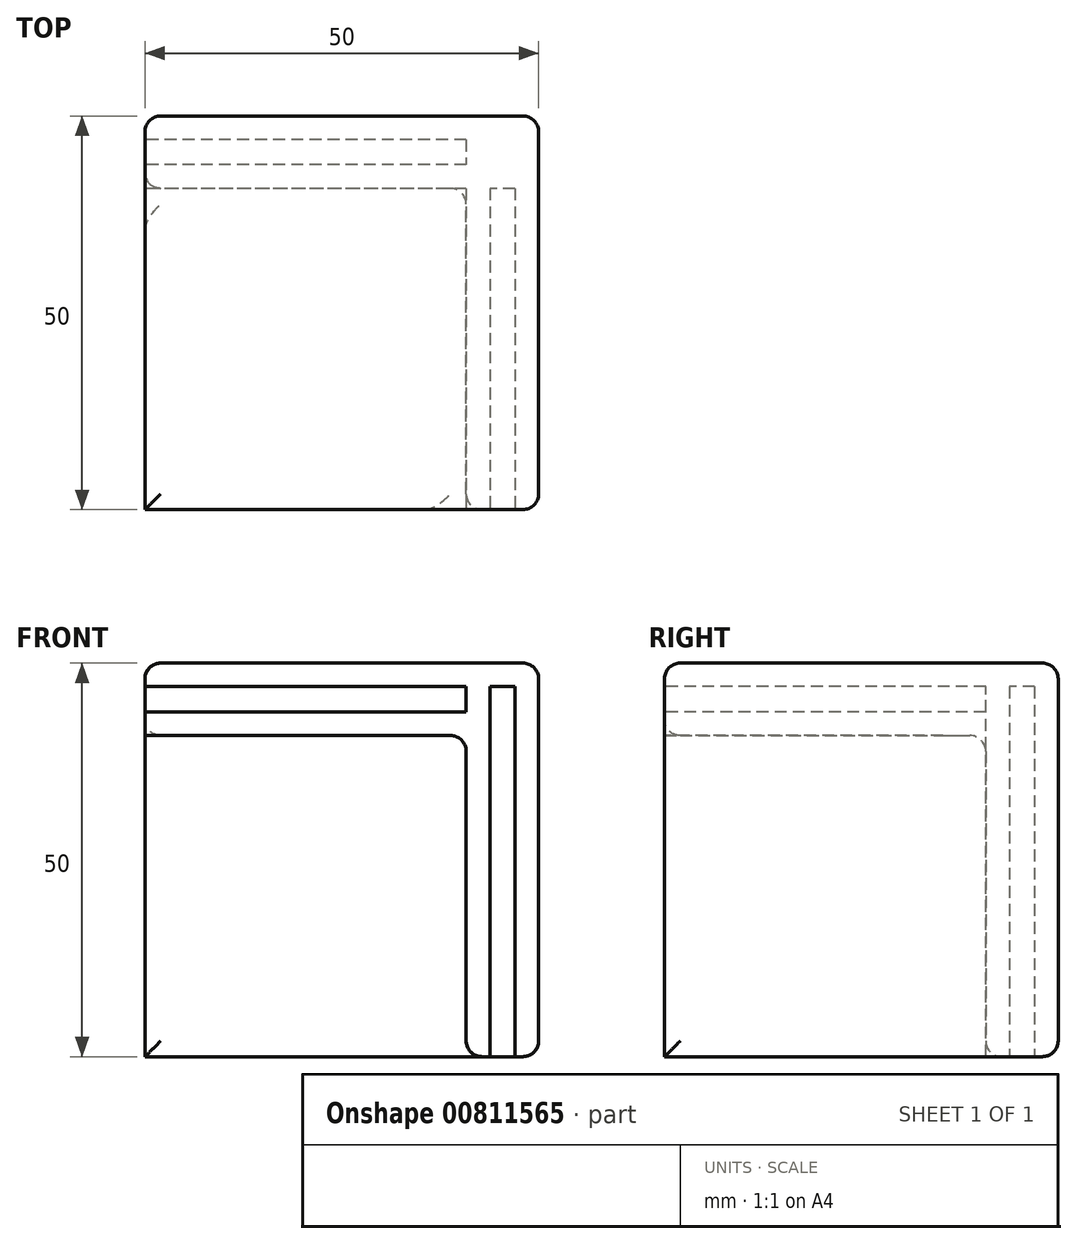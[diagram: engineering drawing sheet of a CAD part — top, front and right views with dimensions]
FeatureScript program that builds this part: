
annotation { "Feature Type Name" : "Feature", "Feature Type Description" : "" }
export const myFeature = defineFeature(function(context is Context, id is Id, definition is map)
    precondition{}
    {
        {
            var Q0;
            Q0=qCreatedBy(makeId("Top.planeOp"),FACE);
            var sketch = newSketch(context, id + "F0", { "sketchPlane" : qUnion([Q0])});
            skLineSegment(sketch, "E0.bottom", {"start": v(25, -25) * mm, "end": v(-25, -25) * mm});
            skLineSegment(sketch, "E0.top", {"start": v(25, 25) * mm, "end": v(-25, 25) * mm});
            skLineSegment(sketch, "E0.left", {"start": v(25, -25) * mm, "end": v(25, 25) * mm});
            skLineSegment(sketch, "E0.right", {"start": v(-25, -25) * mm, "end": v(-25, 25) * mm});
            skPoint(sketch, "E0.middle", {"position": v(0, 0) * mm});
            skSolve(sketch);
        }
        {
            var Q0;
            Q0=makeQuery(id+"F0.imprint","IMPRINT",FACE,{"disambiguationData":[TD([[makeQuery(id+"F0.imprint","IMPRINT",EDGE,{"derivedFrom":sQuery(id+"F0.wireOp",EDGE,"E0.bottom")}),-1.0]])]});
            extrude(context, id + "F1", {"entities" : qUnion([Q0]), "depth" : 3 * mm, "offsetDistance" : 25 * mm});
        }
        {
            var Q0;
            Q0=makeQuery(id+"F1.opExtrude","SWEPT_FACE",FACE,{"disambiguationData":[OSD([sQuery(id+"F0.wireOp",EDGE,"E0.right")])]});
            var sketch = newSketch(context, id + "F2", { "sketchPlane" : qUnion([Q0])});
            skLineSegment(sketch, "E1.bottom", {"start": v(-25, 3) * mm, "end": v(-22, 3) * mm});
            skLineSegment(sketch, "E1.top", {"start": v(-25, -47) * mm, "end": v(-22, -47) * mm});
            skLineSegment(sketch, "E1.left", {"start": v(-25, 3) * mm, "end": v(-25, -47) * mm});
            skLineSegment(sketch, "E1.right", {"start": v(-22, 3) * mm, "end": v(-22, -47) * mm});
            skLineSegment(sketch, "E2.bottom", {"start": v(-18.8, 3) * mm, "end": v(-15.8, 3) * mm});
            skLineSegment(sketch, "E2.top", {"start": v(-18.8, -47) * mm, "end": v(-15.8, -47) * mm});
            skLineSegment(sketch, "E2.left", {"start": v(-18.8, 3) * mm, "end": v(-18.8, -47) * mm});
            skLineSegment(sketch, "E2.right", {"start": v(-15.8, 3) * mm, "end": v(-15.8, -47) * mm});
            skSolve(sketch);
        }
        {
            var Q0;
            {var subQ0=sQuery(id+"F2.wireOp",EDGE,"E1.bottom");Q0=makeQuery(id+"F2.imprint","IMPRINT",FACE,{"disambiguationData":[TD([[makeQuery(id+"F2.imprint","IMPRINT",EDGE,{"derivedFrom":subQ0}),1.0]])]});}
            var Q1;
            {var subQ0=sQuery(id+"F2.wireOp",EDGE,"E2.bottom");Q1=makeQuery(id+"F2.imprint","IMPRINT",FACE,{"disambiguationData":[TD([[makeQuery(id+"F2.imprint","IMPRINT",EDGE,{"derivedFrom":subQ0}),1.0]])]});}
            var Q2;
            {var subQ0=sQuery(id+"F2.wireOp",EDGE,"E2.top");Q2=makeQuery(id+"F2.imprint","IMPRINT",FACE,{"disambiguationData":[TD([[makeQuery(id+"F2.imprint","IMPRINT",EDGE,{"derivedFrom":subQ0}),1.0]])]});}
            var Q3;
            {var subQ0=sQuery(id+"F2.wireOp",EDGE,"E1.top");Q3=makeQuery(id+"F2.imprint","IMPRINT",FACE,{"disambiguationData":[TD([[makeQuery(id+"F2.imprint","IMPRINT",EDGE,{"derivedFrom":subQ0}),1.0]])]});}
            var Q4;
            Q4=makeQuery(id+"F1.opExtrude","SWEPT_FACE",FACE,{"disambiguationData":[OSD([sQuery(id+"F0.wireOp",EDGE,"E0.left")])]});
            extrude(context, id + "F3", {"entities" : qUnion([Q0, Q1, Q2, Q3]), "operationType" : NewBodyOperationType.ADD, "endBound" : BoundingType.UP_TO_SURFACE, "oppositeDirection" : true, "depth" : 25 * mm, "endBoundEntityFace" : qUnion([Q4]), "offsetDistance" : 25 * mm});
        }
        {
            var Q0;
            Q0=makeQuery(id+"F1.opExtrude","SWEPT_FACE",FACE,{"disambiguationData":[OSD([sQuery(id+"F0.wireOp",EDGE,"E0.bottom")])]});
            var sketch = newSketch(context, id + "F4", { "sketchPlane" : qUnion([Q0])});
            skLineSegment(sketch, "E3.bottom", {"start": v(25, 3) * mm, "end": v(22, 3) * mm});
            skLineSegment(sketch, "E3.top", {"start": v(25, -47) * mm, "end": v(22, -47) * mm});
            skLineSegment(sketch, "E3.left", {"start": v(25, 3) * mm, "end": v(25, -47) * mm});
            skLineSegment(sketch, "E3.right", {"start": v(22, 3) * mm, "end": v(22, -47) * mm});
            skLineSegment(sketch, "E4.bottom", {"start": v(18.8, 3) * mm, "end": v(15.8, 3) * mm});
            skLineSegment(sketch, "E4.top", {"start": v(18.8, -47) * mm, "end": v(15.8, -47) * mm});
            skLineSegment(sketch, "E4.left", {"start": v(18.8, 3) * mm, "end": v(18.8, -47) * mm});
            skLineSegment(sketch, "E4.right", {"start": v(15.8, 3) * mm, "end": v(15.8, -47) * mm});
            skSolve(sketch);
        }
        {
            var Q0;
            Q0 = qSketchRegion(id + "F4", true);
            var Q1;
            Q1=makeQuery(id+"F3.opExtrude","SWEPT_FACE",FACE,{"disambiguationData":[OSD([sQuery(id+"F2.wireOp",EDGE,"E1.right")])]});
            extrude(context, id + "F5", {"entities" : qUnion([Q0]), "operationType" : NewBodyOperationType.ADD, "endBound" : BoundingType.UP_TO_SURFACE, "oppositeDirection" : true, "depth" : 25 * mm, "endBoundEntityFace" : qUnion([Q1]), "offsetDistance" : 25 * mm});
        }
        {
            var Q0;
            {var subQ0=sQuery(id+"F2.wireOp",EDGE,"E1.right");var subQ1=makeQuery(id+"F3.opExtrude","SWEPT_FACE",FACE,{"disambiguationData":[OSD([subQ0])]});var subQ7=sQuery(id+"F0.wireOp",EDGE,"E0.right");var subQ8=sQuery(id+"F0.wireOp",EDGE,"E0.left");Q0=makeQuery(id+"F5.boolean.opBoolean","SPLIT",FACE,{"disambiguationData":[TD([makeQuery(id+"F5.opExtrude","SWEPT_FACE",FACE,{"disambiguationData":[OSD([sQuery(id+"F4.wireOp",EDGE,"E3.right")])]})])],"derivedFrom":makeQuery(id+"F3.boolean.opBoolean","SPLIT",FACE,{"disambiguationData":[TD([subQ1])],"derivedFrom":makeQuery(id+"F1.opExtrude","CAP_FACE",FACE,{"disambiguationData":[OSD([sQuery(id+"F0.wireOp",EDGE,"E0.bottom"),sQuery(id+"F0.wireOp",EDGE,"E0.top"),subQ8,subQ7])],"isStart":true})})});}
            var Q1;
            Q1=makeQuery(id+"F1.opExtrude","CAP_FACE",FACE,{"disambiguationData":[OSD([sQuery(id+"F0.wireOp",EDGE,"E0.bottom"),sQuery(id+"F0.wireOp",EDGE,"E0.top"),sQuery(id+"F0.wireOp",EDGE,"E0.left"),sQuery(id+"F0.wireOp",EDGE,"E0.right")])],"isStart":false});
            extrude(context, id + "F6", {"entities" : qUnion([Q0]), "operationType" : NewBodyOperationType.ADD, "endBound" : BoundingType.UP_TO_SURFACE, "oppositeDirection" : true, "depth" : 25 * mm, "endBoundEntityFace" : qUnion([Q1]), "offsetDistance" : 25 * mm});
        }
        {
            var Q0;
            Q0=makeQuery(id+"F5.boolean.opBoolean","MERGE",FACE,{"derivedFrom":[makeQuery(id+"F3.opExtrude","SWEPT_FACE",FACE,{"disambiguationData":[OSD([sQuery(id+"F2.wireOp",EDGE,"E1.top")])]}),makeQuery(id+"F3.opExtrude","SWEPT_FACE",FACE,{"disambiguationData":[OSD([sQuery(id+"F2.wireOp",EDGE,"E2.top")])]}),makeQuery(id+"F5.opExtrude","SWEPT_FACE",FACE,{"disambiguationData":[OSD([sQuery(id+"F4.wireOp",EDGE,"E3.top")])]}),makeQuery(id+"F5.opExtrude","SWEPT_FACE",FACE,{"disambiguationData":[OSD([sQuery(id+"F4.wireOp",EDGE,"E4.top")])]})]});
            var sketch = newSketch(context, id + "F7", { "sketchPlane" : qUnion([Q0])});
            skLineSegment(sketch, "E5.bottom", {"start": v(22, -18.8) * mm, "end": v(18.8, -18.8) * mm});
            skLineSegment(sketch, "E5.top", {"start": v(22, -22) * mm, "end": v(18.8, -22) * mm});
            skLineSegment(sketch, "E5.left", {"start": v(22, -18.8) * mm, "end": v(22, -22) * mm});
            skLineSegment(sketch, "E5.right", {"start": v(18.8, -18.8) * mm, "end": v(18.8, -22) * mm});
            skSolve(sketch);
        }
        {
            var Q0;
            Q0 = qSketchRegion(id + "F7", true);
            var Q1;
            Q1=makeQuery(id+"F1.opExtrude","CAP_FACE",FACE,{"disambiguationData":[OSD([sQuery(id+"F0.wireOp",EDGE,"E0.bottom"),sQuery(id+"F0.wireOp",EDGE,"E0.top"),sQuery(id+"F0.wireOp",EDGE,"E0.left"),sQuery(id+"F0.wireOp",EDGE,"E0.right")])],"isStart":false});
            extrude(context, id + "F8", {"entities" : qUnion([Q0]), "operationType" : NewBodyOperationType.ADD, "endBound" : BoundingType.UP_TO_SURFACE, "oppositeDirection" : true, "depth" : 25 * mm, "endBoundEntityFace" : qUnion([Q1]), "offsetDistance" : 25 * mm});
        }
        {
            var Q0;
            Q0=makeQuery(id+"F3.boolean.opBoolean","MERGE",FACE,{"derivedFrom":[makeQuery(id+"F1.opExtrude","SWEPT_FACE",FACE,{"disambiguationData":[OSD([sQuery(id+"F0.wireOp",EDGE,"E0.right")])]}),makeQuery(id+"F3.opExtrude","CAP_FACE",FACE,{"disambiguationData":[OSD([sQuery(id+"F2.wireOp",EDGE,"E1.bottom"),sQuery(id+"F2.wireOp",EDGE,"E1.top"),sQuery(id+"F2.wireOp",EDGE,"E1.left"),sQuery(id+"F2.wireOp",EDGE,"E1.right")])],"isStart":true}),makeQuery(id+"F3.opExtrude","CAP_FACE",FACE,{"disambiguationData":[OSD([sQuery(id+"F2.wireOp",EDGE,"E2.bottom"),sQuery(id+"F2.wireOp",EDGE,"E2.top"),sQuery(id+"F2.wireOp",EDGE,"E2.left"),sQuery(id+"F2.wireOp",EDGE,"E2.right")])],"isStart":true})]});
            var sketch = newSketch(context, id + "F9", { "sketchPlane" : qUnion([Q0])});
            skLineSegment(sketch, "E6.bottom", {"start": v(-15.8, -3.2) * mm, "end": v(25, -3.2) * mm});
            skLineSegment(sketch, "E6.top", {"start": v(-15.8, -6.2) * mm, "end": v(25, -6.2) * mm});
            skLineSegment(sketch, "E6.left", {"start": v(-15.8, -3.2) * mm, "end": v(-15.8, -6.2) * mm});
            skLineSegment(sketch, "E6.right", {"start": v(25, -3.2) * mm, "end": v(25, -6.2) * mm});
            skLineSegment(sketch, "E7.0", {"start": v(25, 0) * mm, "end": v(25, -47) * mm});
            skSolve(sketch);
        }
        {
            var Q0;
            {var subQ0=sQuery(id+"F9.wireOp",EDGE,"E6.bottom");Q0=makeQuery(id+"F9.imprint","IMPRINT",FACE,{"disambiguationData":[TD([[makeQuery(id+"F9.imprint","IMPRINT",EDGE,{"derivedFrom":subQ0}),-1.0]])]});}
            var Q1;
            {var subQ1=sQuery(id+"F0.wireOp",EDGE,"E0.bottom");var subQ3=sQuery(id+"F4.wireOp",EDGE,"E4.right");Q1=makeQuery(id+"F5.boolean.opBoolean","SPLIT",FACE,{"disambiguationData":[TD([makeQuery(id+"F1.opExtrude","SWEPT_FACE",FACE,{"disambiguationData":[OSD([subQ1])]})])],"derivedFrom":makeQuery(id+"F5.opExtrude","SWEPT_FACE",FACE,{"disambiguationData":[OSD([subQ3])]})});}
            extrude(context, id + "F10", {"entities" : qUnion([Q0]), "operationType" : NewBodyOperationType.ADD, "endBound" : BoundingType.UP_TO_SURFACE, "oppositeDirection" : true, "depth" : 25 * mm, "endBoundEntityFace" : qUnion([Q1]), "offsetDistance" : 25 * mm});
        }
        {
            var Q0;
            Q0=makeQuery(id+"F1.opExtrude","CAP_EDGE",EDGE,{"disambiguationData":[OSD([sQuery(id+"F0.wireOp",EDGE,"E0.right")])],"isStart":false});
            var Q1;
            Q1=makeQuery(id+"F1.opExtrude","CAP_EDGE",EDGE,{"disambiguationData":[OSD([sQuery(id+"F0.wireOp",EDGE,"E0.bottom")])],"isStart":false});
            var Q2;
            Q2=makeQuery(id+"F1.opExtrude","CAP_EDGE",EDGE,{"disambiguationData":[OSD([sQuery(id+"F0.wireOp",EDGE,"E0.top")])],"isStart":false});
            var Q3;
            Q3=makeQuery(id+"F1.opExtrude","CAP_EDGE",EDGE,{"disambiguationData":[OSD([sQuery(id+"F0.wireOp",EDGE,"E0.left")])],"isStart":false});
            var Q4;
            Q4=makeQuery(id+"F5.boolean.opBoolean","MERGE",FACE,{"derivedFrom":[makeQuery(id+"F3.boolean.opBoolean","MERGE",FACE,{"derivedFrom":[makeQuery(id+"F1.opExtrude","SWEPT_FACE",FACE,{"disambiguationData":[OSD([sQuery(id+"F0.wireOp",EDGE,"E0.left")])]}),makeQuery(id+"F3.opExtrude","CAP_FACE",FACE,{"disambiguationData":[OSD([sQuery(id+"F2.wireOp",EDGE,"E1.bottom"),sQuery(id+"F2.wireOp",EDGE,"E1.top"),sQuery(id+"F2.wireOp",EDGE,"E1.left"),sQuery(id+"F2.wireOp",EDGE,"E1.right")])],"isStart":false}),makeQuery(id+"F3.opExtrude","CAP_FACE",FACE,{"disambiguationData":[OSD([sQuery(id+"F2.wireOp",EDGE,"E2.bottom"),sQuery(id+"F2.wireOp",EDGE,"E2.top"),sQuery(id+"F2.wireOp",EDGE,"E2.left"),sQuery(id+"F2.wireOp",EDGE,"E2.right")])],"isStart":false})]}),makeQuery(id+"F5.opExtrude","SWEPT_FACE",FACE,{"disambiguationData":[OSD([sQuery(id+"F4.wireOp",EDGE,"E3.left")])]})]});
            var Q5;
            Q5=makeQuery(id+"F3.boolean.opBoolean","MERGE",FACE,{"derivedFrom":[makeQuery(id+"F1.opExtrude","SWEPT_FACE",FACE,{"disambiguationData":[OSD([sQuery(id+"F0.wireOp",EDGE,"E0.top")])]}),makeQuery(id+"F3.opExtrude","SWEPT_FACE",FACE,{"disambiguationData":[OSD([sQuery(id+"F2.wireOp",EDGE,"E1.left")])]})]});
            var Q6;
            {var subQ1=sQuery(id+"F4.wireOp",EDGE,"E4.right");var subQ7=sQuery(id+"F0.wireOp",EDGE,"E0.bottom");var subQ8=makeQuery(id+"F1.opExtrude","SWEPT_FACE",FACE,{"disambiguationData":[OSD([subQ7])]});var subQ10=makeQuery(id+"F3.opExtrude","SWEPT_FACE",FACE,{"disambiguationData":[OSD([sQuery(id+"F2.wireOp",EDGE,"E1.top")])]});Q6=makeQuery(id+"F10.boolean.opBoolean","SPLIT",FACE,{"disambiguationData":[TD([subQ10])],"derivedFrom":makeQuery(id+"F5.boolean.opBoolean","SPLIT",FACE,{"disambiguationData":[TD([subQ8])],"derivedFrom":makeQuery(id+"F5.opExtrude","SWEPT_FACE",FACE,{"disambiguationData":[OSD([subQ1])]})})});}
            var Q7;
            {var subQ1=sQuery(id+"F2.wireOp",EDGE,"E2.right");var subQ5=sQuery(id+"F0.wireOp",EDGE,"E0.right");var subQ6=makeQuery(id+"F1.opExtrude","SWEPT_FACE",FACE,{"disambiguationData":[OSD([subQ5])]});var subQ7=sQuery(id+"F2.wireOp",EDGE,"E1.top");var subQ12=makeQuery(id+"F3.opExtrude","SWEPT_FACE",FACE,{"disambiguationData":[OSD([subQ7])]});Q7=makeQuery(id+"F10.boolean.opBoolean","SPLIT",FACE,{"disambiguationData":[TD([subQ12])],"derivedFrom":makeQuery(id+"F5.boolean.opBoolean","SPLIT",FACE,{"disambiguationData":[TD([subQ6])],"derivedFrom":makeQuery(id+"F3.opExtrude","SWEPT_FACE",FACE,{"disambiguationData":[OSD([subQ1])]})})});}
            fillet(context, id + "F11", {"entities" : qUnion([Q0, Q1, Q2, Q3, Q4, Q5, Q6, Q7]), "radius" : 2 * mm, "tangentPropagation" : true, "allowEdgeOverflow" : false});
        }
    });
